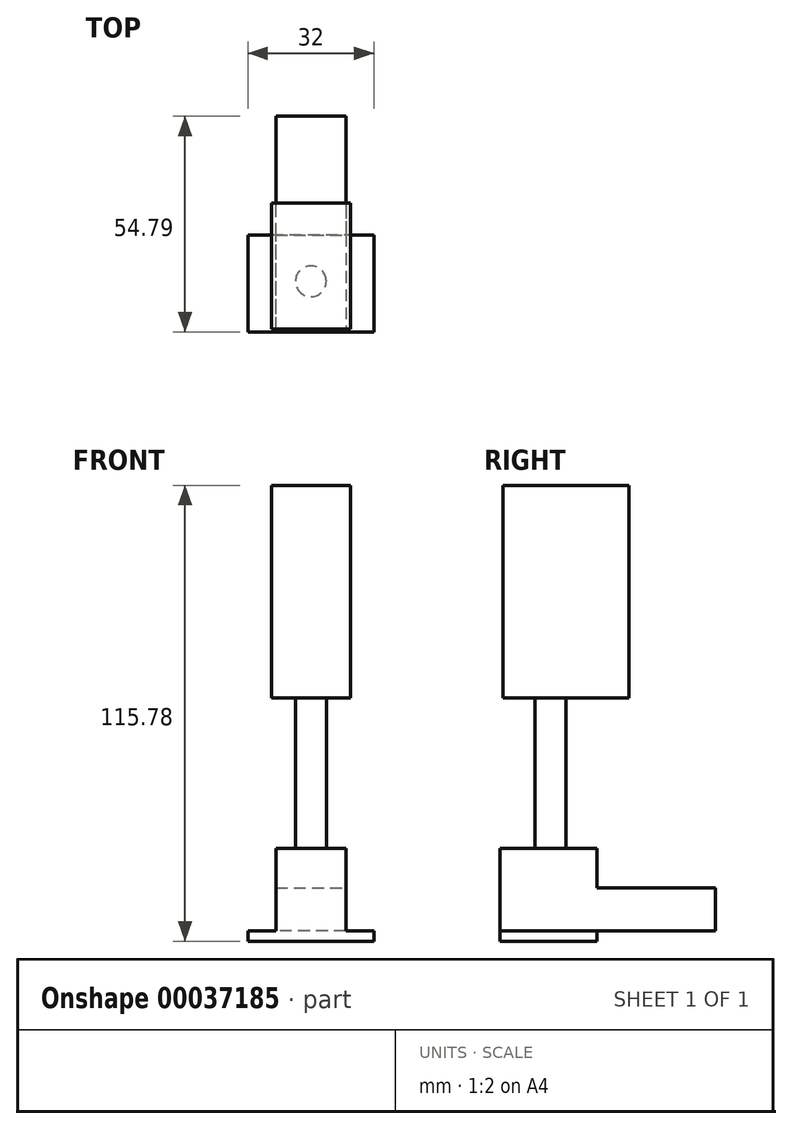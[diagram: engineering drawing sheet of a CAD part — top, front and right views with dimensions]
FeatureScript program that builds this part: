
annotation { "Feature Type Name" : "Feature", "Feature Type Description" : "" }
export const myFeature = defineFeature(function(context is Context, id is Id, definition is map)
    precondition{}
    {
        {
            var Q0;
            Q0=qCreatedBy(makeId("Top.planeOp"),FACE);
            var sketch = newSketch(context, id + "F0", { "sketchPlane" : qUnion([Q0])});
            skLineSegment(sketch, "E0", {"start": v(0, 0) * mm, "end": v(-16, 0) * mm});
            skLineSegment(sketch, "E1", {"start": v(-16, 0) * mm, "end": v(-16, 24.63) * mm});
            skLineSegment(sketch, "E2", {"start": v(-16, 24.63) * mm, "end": v(0, 24.63) * mm});
            skLineSegment(sketch, "E3", {"start": v(0, 0) * mm, "end": v(16, 0) * mm});
            skLineSegment(sketch, "E4", {"start": v(16, 0) * mm, "end": v(16, 24.63) * mm});
            skLineSegment(sketch, "E5", {"start": v(16, 24.63) * mm, "end": v(0, 24.63) * mm});
            skSolve(sketch);
        }
        {
            var Q0;
            Q0=makeQuery(id+"F0.imprint","IMPRINT",FACE,{"disambiguationData":[TD([[makeQuery(id+"F0.imprint","IMPRINT",EDGE,{"derivedFrom":sQuery(id+"F0.wireOp",EDGE,"E0")}),-1.0]])]});
            extrude(context, id + "F1", {"entities" : qUnion([Q0]), "oppositeDirection" : true, "depth" : 2.6 * mm});
        }
        {
            var Q0;
            Q0=qCreatedBy(makeId("Top.planeOp"),FACE);
            var sketch = newSketch(context, id + "F2", { "sketchPlane" : qUnion([Q0])});
            skLineSegment(sketch, "E6", {"start": v(0, 0) * mm, "end": v(8.92, 0) * mm});
            skLineSegment(sketch, "E7", {"start": v(0, 0) * mm, "end": v(-8.92, 0) * mm});
            skLineSegment(sketch, "E8", {"start": v(-8.92, 0) * mm, "end": v(-8.92, 54.8) * mm});
            skLineSegment(sketch, "E9", {"start": v(-8.92, 54.8) * mm, "end": v(8.92, 54.8) * mm});
            skLineSegment(sketch, "E10", {"start": v(8.92, 54.8) * mm, "end": v(8.92, 0) * mm});
            skSolve(sketch);
        }
        {
            var Q0;
            Q0 = qSketchRegion(id + "F2", true);
            extrude(context, id + "F3", {"entities" : qUnion([Q0]), "operationType" : NewBodyOperationType.ADD, "depth" : 11 * mm});
        }
        {
            var Q0;
            Q0=qCreatedBy(makeId("Top.planeOp"),FACE);
            cPlane(context, id + "F4", {"entities" : qUnion([Q0]), "cplaneType" : CPlaneType.OFFSET, "offset" : 11 * mm, "width" : 150 * mm, "height" : 150 * mm});
        }
        {
            var Q0;
            Q0=qCreatedBy(id+"F4.planeOp",FACE);
            var sketch = newSketch(context, id + "F5", { "sketchPlane" : qUnion([Q0])});
            skLineSegment(sketch, "E11", {"start": v(0, 0) * mm, "end": v(-8.92, 0) * mm});
            skLineSegment(sketch, "E12", {"start": v(-8.92, 0) * mm, "end": v(-8.92, 24.63) * mm});
            skLineSegment(sketch, "E13", {"start": v(-8.92, 24.63) * mm, "end": v(8.92, 24.63) * mm});
            skLineSegment(sketch, "E14", {"start": v(8.92, 24.63) * mm, "end": v(8.92, 0) * mm});
            skLineSegment(sketch, "E15", {"start": v(0, 0) * mm, "end": v(8.92, 0) * mm});
            skLineSegment(sketch, "E16", {"start": v(8.92, 0) * mm, "end": v(8.92, 24.63) * mm});
            skSolve(sketch);
        }
        {
            var Q0;
            Q0 = qSketchRegion(id + "F5", true);
            extrude(context, id + "F6", {"entities" : qUnion([Q0]), "operationType" : NewBodyOperationType.ADD, "depth" : 10 * mm});
        }
        {
            var Q0;
            Q0=qCreatedBy(makeId("Top.planeOp"),FACE);
            cPlane(context, id + "F7", {"entities" : qUnion([Q0]), "cplaneType" : CPlaneType.OFFSET, "offset" : 21 * mm, "width" : 150 * mm, "height" : 150 * mm});
        }
        {
            var Q0;
            Q0=qCreatedBy(id+"F7.planeOp",FACE);
            var sketch = newSketch(context, id + "F8", { "sketchPlane" : qUnion([Q0])});
            skLineSegment(sketch, "E17", {"start": v(0, 0) * mm, "end": v(0, 12.88) * mm});
            skCircle(sketch, "E18", {"center": v(0, 12.88) * mm, "radius": 3.91 * mm});
            skSolve(sketch);
        }
        {
            var Q0;
            Q0 = qSketchRegion(id + "F8", true);
            extrude(context, id + "F9", {"entities" : qUnion([Q0]), "depth" : 59.18 * mm});
        }
        {
            var Q0;
            Q0=qCreatedBy(makeId("Top.planeOp"),FACE);
            cPlane(context, id + "F10", {"entities" : qUnion([Q0]), "cplaneType" : CPlaneType.OFFSET, "offset" : 59.18 * mm, "width" : 150 * mm, "height" : 150 * mm});
        }
        {
            var Q0;
            Q0=qCreatedBy(id+"F10.planeOp",FACE);
            var sketch = newSketch(context, id + "F11", { "sketchPlane" : qUnion([Q0])});
            skLineSegment(sketch, "E19.0", {"start": v(0, 0.75) * mm, "end": v(-10, 0.75) * mm});
            skLineSegment(sketch, "E20.0", {"start": v(0, 0.75) * mm, "end": v(10, 0.75) * mm});
            skLineSegment(sketch, "E21.0", {"start": v(0, 32.75) * mm, "end": v(-10, 32.75) * mm});
            skLineSegment(sketch, "E22.0", {"start": v(0, 32.75) * mm, "end": v(10, 32.75) * mm});
            skLineSegment(sketch, "E23", {"start": v(-10, 32.75) * mm, "end": v(-10, 0.75) * mm});
            skLineSegment(sketch, "E24", {"start": v(10, 0.75) * mm, "end": v(10, 32.75) * mm});
            skSolve(sketch);
        }
        {
            var Q0;
            Q0 = qSketchRegion(id + "F11", true);
            extrude(context, id + "F12", {"entities" : qUnion([Q0]), "operationType" : NewBodyOperationType.ADD, "depth" : 54 * mm});
        }
    });
